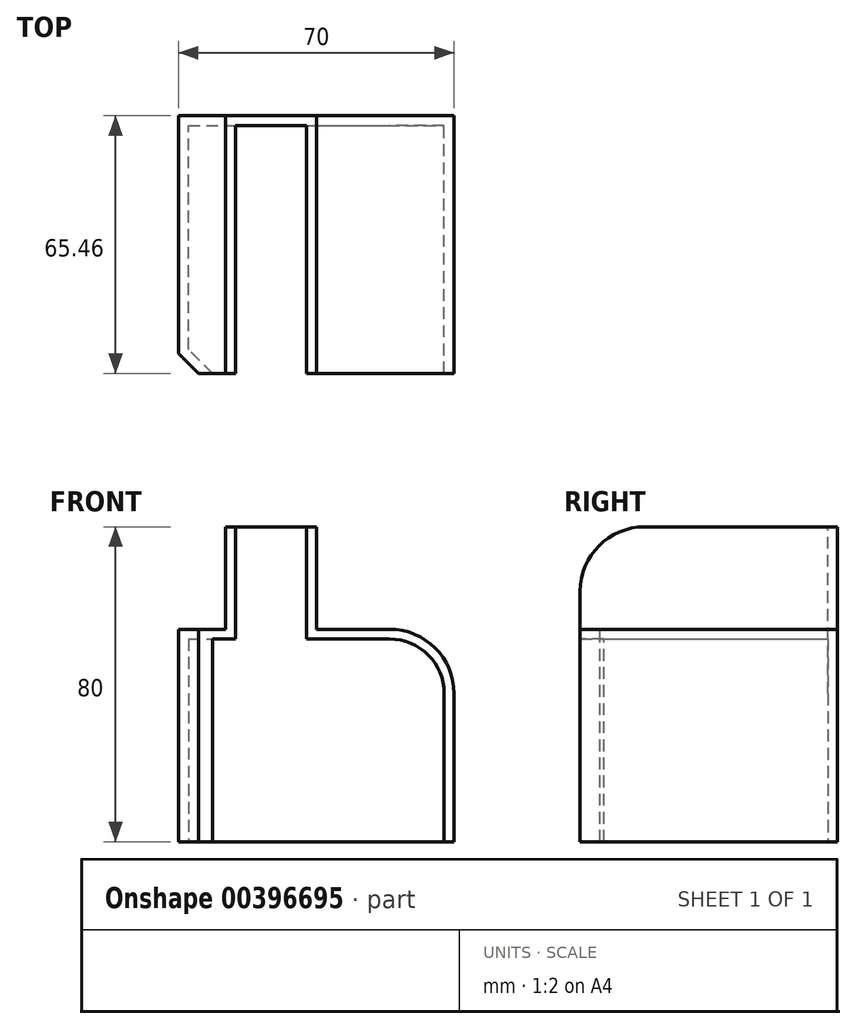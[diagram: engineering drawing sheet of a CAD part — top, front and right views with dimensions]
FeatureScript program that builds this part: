
annotation { "Feature Type Name" : "Feature", "Feature Type Description" : "" }
export const myFeature = defineFeature(function(context is Context, id is Id, definition is map)
    precondition{}
    {
        {
            var Q0;
            Q0=qCreatedBy(makeId("Front.planeOp"),FACE);
            var sketch = newSketch(context, id + "F0", { "sketchPlane" : qUnion([Q0])});
            skLineSegment(sketch, "E0.bottom", {"start": v(-30, 24) * mm, "end": v(40, 24) * mm});
            skLineSegment(sketch, "E0.top", {"start": v(-30, -30) * mm, "end": v(40, -30) * mm});
            skLineSegment(sketch, "E0.left", {"start": v(-30, 24) * mm, "end": v(-30, -30) * mm});
            skLineSegment(sketch, "E0.right", {"start": v(40, 24) * mm, "end": v(40, -30) * mm});
            skLineSegment(sketch, "E1.bottom", {"start": v(5, 24) * mm, "end": v(-18, 24) * mm});
            skLineSegment(sketch, "E1.top", {"start": v(5, 50) * mm, "end": v(-18, 50) * mm});
            skLineSegment(sketch, "E1.left", {"start": v(5, 24) * mm, "end": v(5, 50) * mm});
            skLineSegment(sketch, "E1.right", {"start": v(-18, 24) * mm, "end": v(-18, 50) * mm});
            skSolve(sketch);
        }
        {
            var Q0;
            Q0 = qSketchRegion(id + "F0", true);
            extrude(context, id + "F1", {"entities" : qUnion([Q0]), "depth" : 65.46 * mm});
        }
        {
            var Q0;
            Q0=makeQuery(id+"F1.opExtrude","SWEPT_EDGE",EDGE,{"disambiguationData":[OSD([sQuery(id+"F0.wireOp",EDGE,"E0.bottom"),sQuery(id+"F0.wireOp",EDGE,"E0.right")])]});
            var Q1;
            Q1=makeQuery(id+"F1.opExtrude","CAP_EDGE",EDGE,{"disambiguationData":[OSD([sQuery(id+"F0.wireOp",EDGE,"E1.top")])],"isStart":false});
            fillet(context, id + "F2", {"entities" : qUnion([Q0, Q1]), "radius" : 16.37 * mm, "tangentPropagation" : true, "allowEdgeOverflow" : false});
        }
        {
            var Q0;
            Q0=makeQuery(id+"F1.opExtrude","CAP_EDGE",EDGE,{"disambiguationData":[OSD([sQuery(id+"F0.wireOp",EDGE,"E0.left")])],"isStart":false});
            chamfer(context, id + "F3", {"entities" : qUnion([Q0]), "width" : 5.08 * mm, "tangentPropagation" : true});
        }
        {
            var Q0;
            Q0=makeQuery(id+"F1.opExtrude","SWEPT_FACE",FACE,{"disambiguationData":[OSD([sQuery(id+"F0.wireOp",EDGE,"E0.top")])]});
            var Q1;
            Q1=makeQuery(id+"F1.opExtrude","SWEPT_FACE",FACE,{"disambiguationData":[OSD([sQuery(id+"F0.wireOp",EDGE,"E1.top")])]});
            var Q2;
            Q2=makeQuery(id+"F2.opFillet","BLEND_FACE",FACE,{"disambiguationData":[OSD([sQuery(id+"F0.wireOp",EDGE,"E1.top")])]});
            var Q3;
            Q3=makeQuery(id+"F1.opExtrude","CAP_FACE",FACE,{"disambiguationData":[OSD([sQuery(id+"F0.wireOp",EDGE,"E0.bottom"),sQuery(id+"F0.wireOp",EDGE,"E0.top"),sQuery(id+"F0.wireOp",EDGE,"E0.left"),sQuery(id+"F0.wireOp",EDGE,"E0.right"),sQuery(id+"F0.wireOp",EDGE,"E1.top"),sQuery(id+"F0.wireOp",EDGE,"E1.left"),sQuery(id+"F0.wireOp",EDGE,"E1.right")])],"isStart":false});
            shell(context, id + "F4", {"entities" : qUnion([Q0, Q1, Q2, Q3]), "thickness" : 2.5 * mm});
        }
    });
